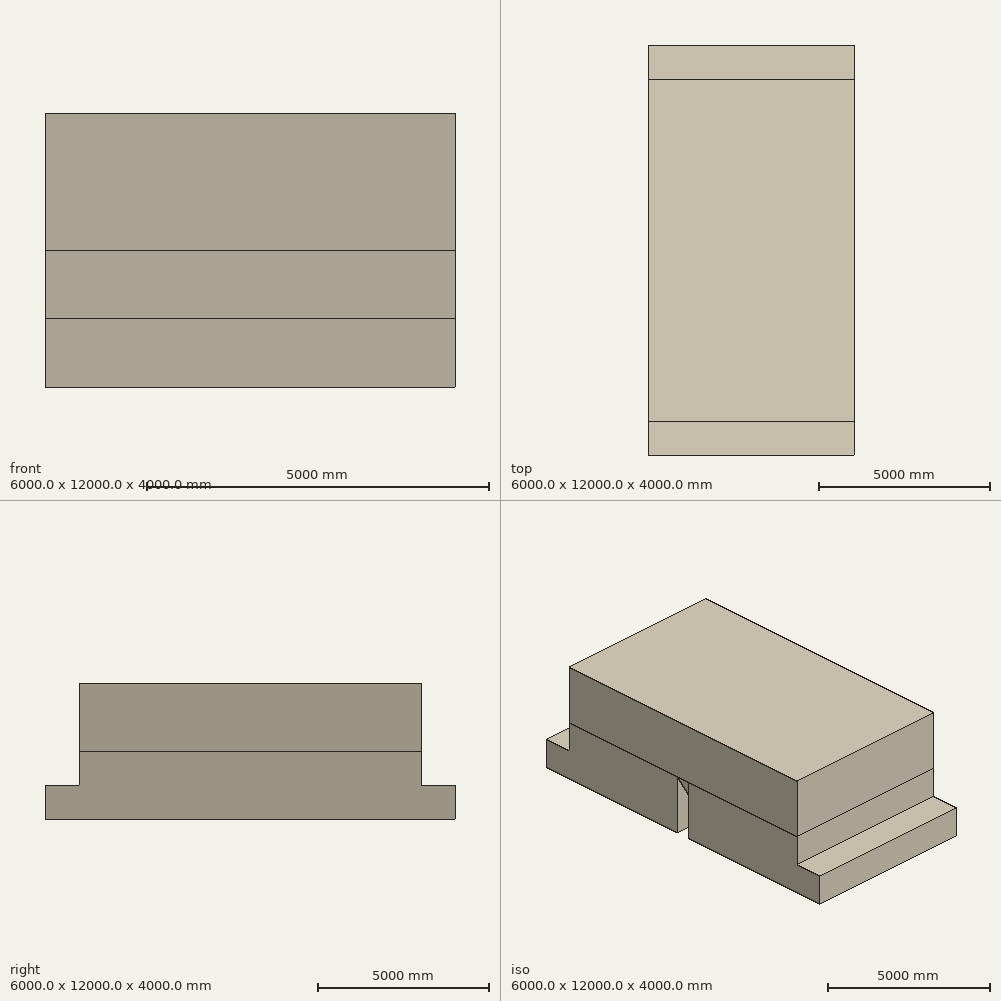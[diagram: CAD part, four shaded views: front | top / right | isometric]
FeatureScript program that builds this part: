
annotation { "Feature Type Name" : "Feature", "Feature Type Description" : "" }
export const myFeature = defineFeature(function(context is Context, id is Id, definition is map)
    precondition{}
    {
        {
            var Q0;
            Q0=qCreatedBy(makeId("Front.planeOp"),FACE);
            var sketch = newSketch(context, id + "F0", { "sketchPlane" : qUnion([Q0])});
            skLineSegment(sketch, "E0.bottom", {"start": v(0, 0) * mm, "end": v(6000, 0) * mm});
            skLineSegment(sketch, "E0.top", {"start": v(0, 2000) * mm, "end": v(6000, 2000) * mm});
            skLineSegment(sketch, "E0.left", {"start": v(0, 0) * mm, "end": v(0, 2000) * mm});
            skLineSegment(sketch, "E0.right", {"start": v(6000, 0) * mm, "end": v(6000, 2000) * mm});
            skSolve(sketch);
        }
        {
            var Q0;
            Q0 = qSketchRegion(id + "F0", true);
            extrude(context, id + "F1", {"entities" : qUnion([Q0]), "depth" : 5000 * mm});
        }
        {
            var Q0;
            Q0=makeQuery(id+"F1.opExtrude","CAP_FACE",FACE,{"disambiguationData":[OSD([sQuery(id+"F0.wireOp",EDGE,"E0.bottom"),sQuery(id+"F0.wireOp",EDGE,"E0.top"),sQuery(id+"F0.wireOp",EDGE,"E0.left"),sQuery(id+"F0.wireOp",EDGE,"E0.right")])],"isStart":true});
            var sketch = newSketch(context, id + "F2", { "sketchPlane" : qUnion([Q0])});
            skLineSegment(sketch, "E1.0", {"start": v(0, 0) * mm, "end": v(0, 2000) * mm});
            skLineSegment(sketch, "E2", {"start": v(0, 0) * mm, "end": v(-1154.7, 0) * mm});
            skLineSegment(sketch, "E3", {"start": v(-1154.7, 0) * mm, "end": v(0, 2000) * mm});
            skLineSegment(sketch, "E4", {"start": v(0, 2000) * mm, "end": v(0, 2000) * mm});
            skSolve(sketch);
        }
        {
            var Q0;
            Q0 = qSketchRegion(id + "F2", true);
            extrude(context, id + "F3", {"entities" : qUnion([Q0]), "operationType" : NewBodyOperationType.REMOVE, "oppositeDirection" : true, "depth" : 250 * mm});
        }
        {
            var Q0;
            Q0=makeQuery(id+"F1.opExtrude","SWEPT_BODY",BODY,{"disambiguationData":[OSD([sQuery(id+"F0.wireOp",EDGE,"E0.bottom"),sQuery(id+"F0.wireOp",EDGE,"E0.top"),sQuery(id+"F0.wireOp",EDGE,"E0.left"),sQuery(id+"F0.wireOp",EDGE,"E0.right")])]});
            var Q1;
            Q1=makeQuery(id+"F1.opExtrude","CAP_FACE",FACE,{"disambiguationData":[OSD([sQuery(id+"F0.wireOp",EDGE,"E0.bottom"),sQuery(id+"F0.wireOp",EDGE,"E0.top"),sQuery(id+"F0.wireOp",EDGE,"E0.left"),sQuery(id+"F0.wireOp",EDGE,"E0.right")])],"isStart":true});
            mirror(context, id + "F4", {"entities" : qUnion([Q0]), "mirrorPlane" : qUnion([Q1])});
        }
        {
            var Q0;
            Q0=makeQuery(id+"F4.opPattern","COPY",BODY,{"derivedFrom":makeQuery(id+"F1.opExtrude","SWEPT_BODY",BODY,{"disambiguationData":[OSD([sQuery(id+"F0.wireOp",EDGE,"E0.bottom"),sQuery(id+"F0.wireOp",EDGE,"E0.top"),sQuery(id+"F0.wireOp",EDGE,"E0.left"),sQuery(id+"F0.wireOp",EDGE,"E0.right")])]}),"instanceName":"1"});
            var Q1;
            Q1=makeQuery(id+"F1.opExtrude","SWEPT_BODY",BODY,{"disambiguationData":[OSD([sQuery(id+"F0.wireOp",EDGE,"E0.bottom"),sQuery(id+"F0.wireOp",EDGE,"E0.top"),sQuery(id+"F0.wireOp",EDGE,"E0.left"),sQuery(id+"F0.wireOp",EDGE,"E0.right")])]});
            booleanBodies(context, id + "F5", {"operationType" : BooleanOperationType.UNION, "tools" : qUnion([Q0, Q1])});
        }
        {
            var Q0;
            {var subQ0=makeQuery(id+"F1.opExtrude","SWEPT_FACE",FACE,{"disambiguationData":[OSD([sQuery(id+"F0.wireOp",EDGE,"E0.top")])]});Q0=makeQuery(id+"F5.opBoolean","MERGE",FACE,{"derivedFrom":[subQ0,makeQuery(id+"F4.opPattern","COPY",FACE,{"derivedFrom":subQ0,"instanceName":"1"})]});}
            extrude(context, id + "F6", {"entities" : qUnion([Q0]), "depth" : 2000 * mm});
        }
        {
            var Q0;
            Q0=makeQuery(id+"F1.opExtrude","CAP_FACE",FACE,{"disambiguationData":[OSD([sQuery(id+"F0.wireOp",EDGE,"E0.bottom"),sQuery(id+"F0.wireOp",EDGE,"E0.top"),sQuery(id+"F0.wireOp",EDGE,"E0.left"),sQuery(id+"F0.wireOp",EDGE,"E0.right")])],"isStart":false});
            var sketch = newSketch(context, id + "F7", { "sketchPlane" : qUnion([Q0])});
            skLineSegment(sketch, "E5.0", {"start": v(0, 0) * mm, "end": v(6000, 0) * mm});
            skLineSegment(sketch, "E6", {"start": v(0, 0) * mm, "end": v(0, 1000) * mm});
            skLineSegment(sketch, "E7", {"start": v(0, 1000) * mm, "end": v(6000, 1000) * mm});
            skLineSegment(sketch, "E8", {"start": v(6000, 1000) * mm, "end": v(6000, 0) * mm});
            skSolve(sketch);
        }
        {
            var Q0;
            Q0=makeQuery(id+"F4.opPattern","COPY",FACE,{"derivedFrom":makeQuery(id+"F1.opExtrude","CAP_FACE",FACE,{"disambiguationData":[OSD([sQuery(id+"F0.wireOp",EDGE,"E0.bottom"),sQuery(id+"F0.wireOp",EDGE,"E0.top"),sQuery(id+"F0.wireOp",EDGE,"E0.left"),sQuery(id+"F0.wireOp",EDGE,"E0.right")])],"isStart":false}),"instanceName":"1"});
            var sketch = newSketch(context, id + "F8", { "sketchPlane" : qUnion([Q0])});
            skLineSegment(sketch, "E9.0", {"start": v(0, 0) * mm, "end": v(-6000, 0) * mm});
            skLineSegment(sketch, "E10", {"start": v(-6000, 0) * mm, "end": v(-6000, 1000) * mm});
            skLineSegment(sketch, "E11", {"start": v(-6000, 1000) * mm, "end": v(0, 1000) * mm});
            skLineSegment(sketch, "E12", {"start": v(0, 1000) * mm, "end": v(0, 0) * mm});
            skSolve(sketch);
        }
        {
            var Q0;
            Q0=makeQuery(id+"F7.imprint","IMPRINT",FACE,{"disambiguationData":[TD([[makeQuery(id+"F7.imprint","IMPRINT",EDGE,{"derivedFrom":sQuery(id+"F7.wireOp",EDGE,"E5.0")}),1.0]])]});
            extrude(context, id + "F9", {"entities" : qUnion([Q0]), "operationType" : NewBodyOperationType.ADD, "depth" : 1000 * mm});
        }
        {
            var Q0;
            Q0 = qSketchRegion(id + "F8", true);
            extrude(context, id + "F10", {"entities" : qUnion([Q0]), "operationType" : NewBodyOperationType.ADD, "depth" : 1000 * mm});
        }
    });
